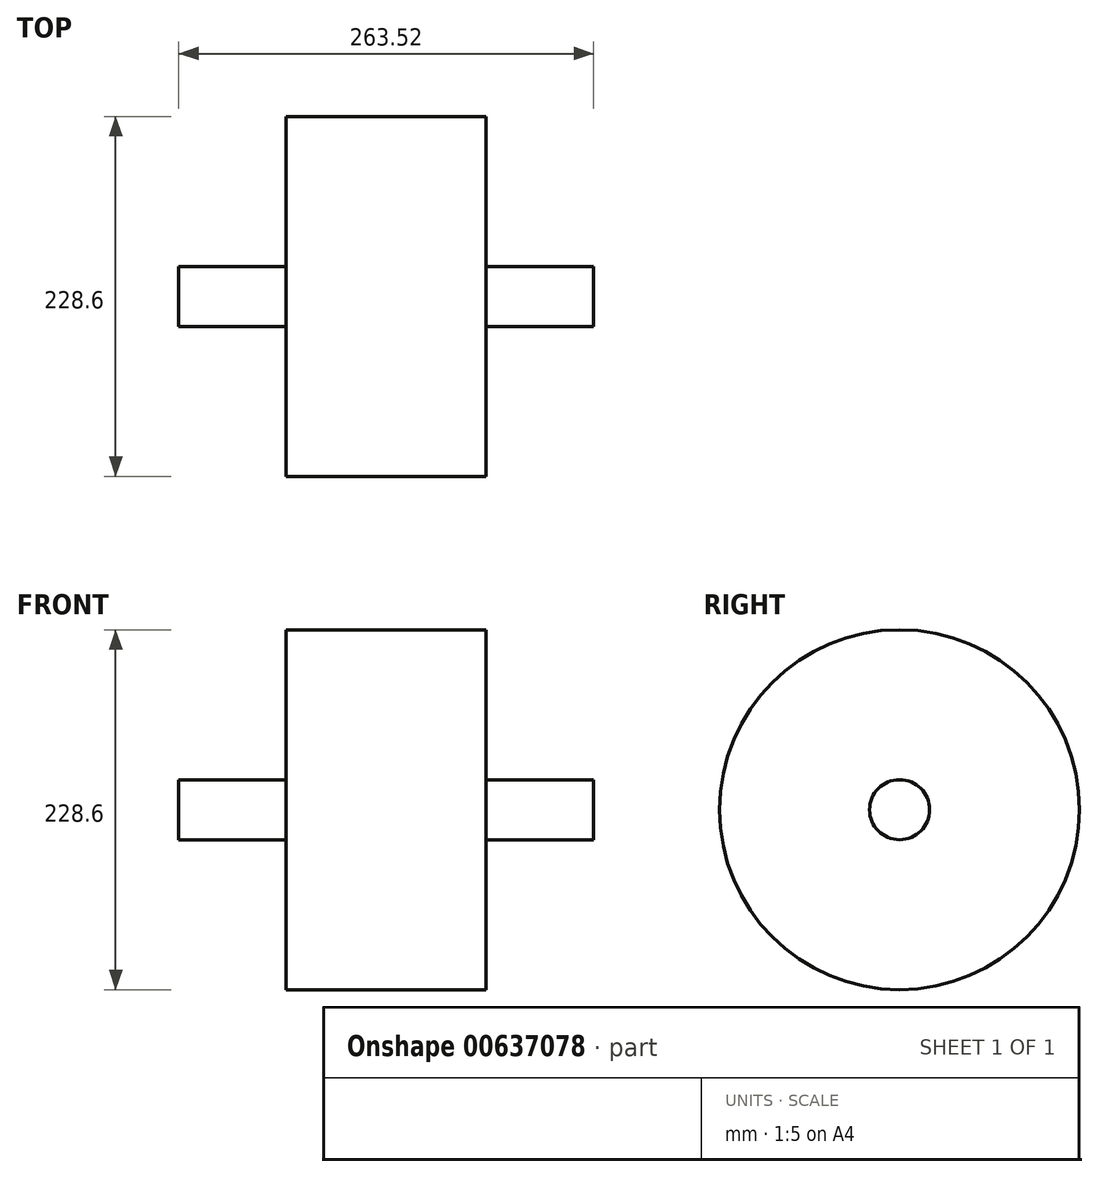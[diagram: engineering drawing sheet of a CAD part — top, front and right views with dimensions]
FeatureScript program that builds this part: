
annotation { "Feature Type Name" : "Feature", "Feature Type Description" : "" }
export const myFeature = defineFeature(function(context is Context, id is Id, definition is map)
    precondition{}
    {
        {
            var Q0;
            Q0=qCreatedBy(makeId("Right.planeOp"),FACE);
            var sketch = newSketch(context, id + "F0", { "sketchPlane" : qUnion([Q0])});
            skCircle(sketch, "E0", {"center": v(0, 0) * mm, "radius": 19.05 * mm});
            skSolve(sketch);
        }
        {
            var Q0;
            Q0=qSketchRegion(id+"F0",true);
            extrude(context, id + "F1", {"entities" : qUnion([Q0]), "endBound" : BoundingType.SYMMETRIC, "depth" : 263.52 * mm, "offsetDistance" : 25.4 * mm});
        }
        {
            var Q0;
            Q0=qCreatedBy(makeId("Right.planeOp"),FACE);
            var sketch = newSketch(context, id + "F2", { "sketchPlane" : qUnion([Q0])});
            skCircle(sketch, "E1", {"center": v(0, 0) * mm, "radius": 114.3 * mm});
            skSolve(sketch);
        }
        {
            var Q0;
            Q0=qSketchRegion(id+"F2",true);
            extrude(context, id + "F3", {"entities" : qUnion([Q0]), "operationType" : NewBodyOperationType.ADD, "endBound" : BoundingType.SYMMETRIC, "depth" : 127 * mm, "offsetDistance" : 25.4 * mm});
        }
    });
